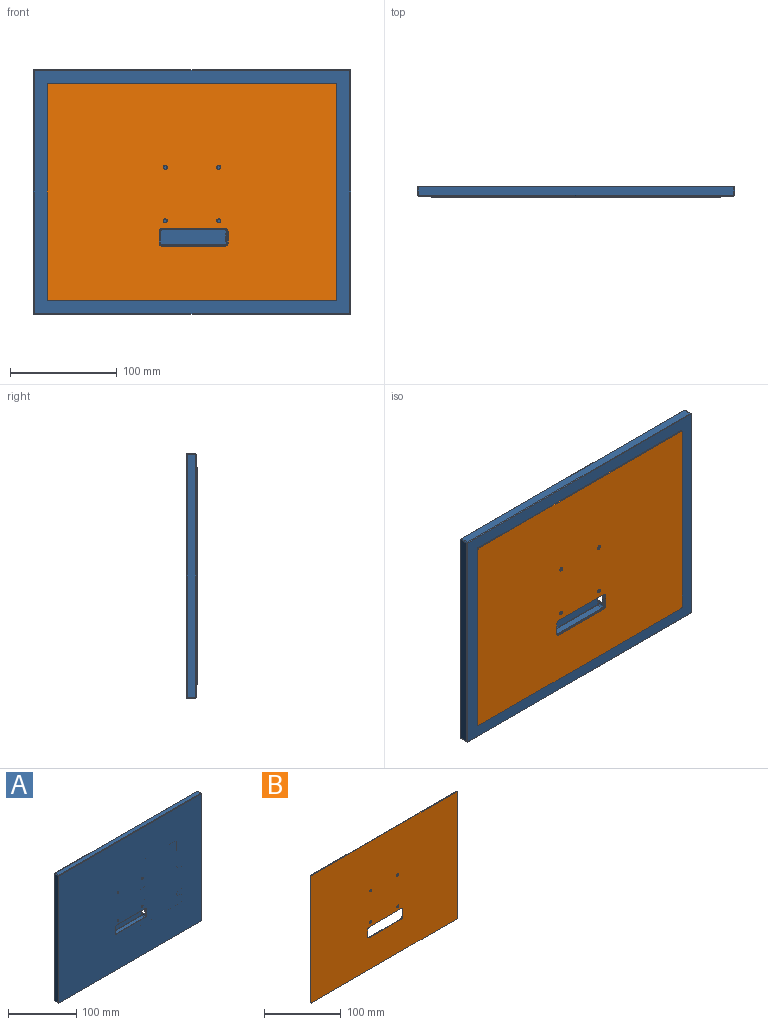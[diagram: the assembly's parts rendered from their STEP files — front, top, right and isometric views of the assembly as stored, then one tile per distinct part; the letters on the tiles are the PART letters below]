
ASSEMBLY  parts=2 mates=1
PART A: 309 faces, bbox 296.4x8.5x228.8 mm
  f0: plane 295.4x227.8mm, normal (0,-1,0), area 66249.3mm2, adj f1,f2,f3,f4,f5,f6,f7,f8
  f1: cone r=0.75mm half-angle=45deg, axis (0,1,0), area 0.8mm2, adj f0,f2,f8,f19
  f2: plane 226.8x0.5mm, normal (-0.71,-0.71,0), area 160.4mm2, adj f0,f1,f3,f20
  f3: cone r=0.75mm half-angle=45deg, axis (0,1,0), area 0.8mm2, adj f0,f2,f4,f21
  f4: plane 294.4x0.5mm, normal (0,-0.71,-0.71), area 208.2mm2, adj f0,f3,f5,f22
  f5: cone r=0.75mm half-angle=45deg, axis (0,1,0), area 0.8mm2, adj f0,f4,f6,f23
  f6: plane 226.8x0.5mm, normal (0.71,-0.71,0), area 160.4mm2, adj f0,f5,f7,f24
  f7: cone r=0.75mm half-angle=45deg, axis (0,1,0), area 0.8mm2, adj f0,f6,f8,f25
  f8: plane 294.4x0.5mm, normal (0,-0.71,0.71), area 208.2mm2, adj f0,f1,f7,f9
  f9: plane 294.4x7.9mm, normal (0,0,1), area 2325.8mm2, adj f8,f10,f19,f25
  f10: plane 294.4x0.1mm, normal (0,0.71,0.71), area 41.6mm2, adj f9,f11,f12,f18
  f11: plane 296.2x228.6mm, normal (0,1,0), area 2101.9mm2, adj f10,f12,f13,f14,f15,f16,f17,f18
  f12: cone r=0.95mm half-angle=45deg, axis (0,-1,0), area 0.2mm2, adj f10,f11,f13,f25
  f13: plane 226.8x0.1mm, normal (0.71,0.71,0), area 32.1mm2, adj f11,f12,f14,f24
  f14: cone r=0.95mm half-angle=45deg, axis (0,-1,0), area 0.2mm2, adj f11,f13,f15,f23
  f15: plane 294.4x0.1mm, normal (0,0.71,-0.71), area 41.6mm2, adj f11,f14,f16,f22
  f16: cone r=0.95mm half-angle=45deg, axis (0,-1,0), area 0.2mm2, adj f11,f15,f17,f21
  f17: plane 226.8x0.1mm, normal (-0.71,0.71,0), area 32.1mm2, adj f11,f16,f18,f20
  f18: cone r=0.95mm half-angle=45deg, axis (0,-1,0), area 0.2mm2, adj f10,f11,f17,f19
  f19: cylinder r=1mm len=7.9mm, axis (0,-1,0), area 12.4mm2, adj f1,f9,f18,f20
  f20: plane 226.8x7.9mm, normal (-1,0,0), area 1791.7mm2, adj f2,f17,f19,f21
  f21: cylinder r=1mm len=7.9mm, axis (0,-1,0), area 12.4mm2, adj f3,f16,f20,f22
  f22: plane 294.4x7.9mm, normal (0,0,-1), area 2325.8mm2, adj f4,f15,f21,f23
  f23: cylinder r=1mm len=7.9mm, axis (0,-1,0), area 12.4mm2, adj f5,f14,f22,f24
  f24: plane 226.8x7.9mm, normal (1,0,0), area 1791.7mm2, adj f6,f13,f23,f25
  f25: cylinder r=1mm len=7.9mm, axis (0,-1,0), area 12.4mm2, adj f7,f9,f12,f24
  f26: plane 34.66x6.82mm, normal (0,0,1), area 181.9mm2, adj f11,f30,f41,f150,f153,f162,f191,f196
  f27: plane 52.54x20.14mm, normal (0,1,0), area 278mm2, adj f35,f36,f38,f39,f40,f169,f187,f192
  f28: plane 41.64x20.14mm, normal (0,1,0), area 234.4mm2, adj f37,f168,f173,f174,f175,f183,f185,f186
  f29: plane 35.59x14.84mm, normal (0,1,0), area 183.9mm2, adj f50,f167,f171,f176,f177,f178,f179,f182
  f30: plane 32.68x31.26mm, normal (0,1,0), area 242.7mm2, adj f26,f150,f170,f189,f190,f191,f193,f236
  f31: plane 53.55x1.8mm, normal (0,1,0), area 92.6mm2, adj f89,f90,f92,f197
  f32: plane 29.26x2.3mm, normal (0,1,0), area 66.4mm2, adj f56,f58,f59,f60,f62,f222,f223,f224
  f33: plane 286.85x170.03mm, normal (0,1,0), area 4919.4mm2, adj f48,f51,f52,f53,f54,f55,f57,f61
  f34: plane 52.85x4.27mm, normal (0,1,0), area 217.9mm2, adj f42,f43,f44,f45,f46,f47,f49,f181
  f35: cylinder r=1mm len=5mm, axis (0,1,0), area 7.9mm2, adj f27,f36,f41,f192
  f36: plane 49.4x5mm, normal (0,0,1), area 247mm2, adj f27,f35,f38,f41
  f37: plane 38.5x5mm, normal (0,0,1), area 192.5mm2, adj f28,f41,f175,f186
  f38: cylinder r=1mm len=5mm, axis (0,-1,0), area 7.9mm2, adj f27,f36,f39,f41
  f39: plane 17.74x5mm, normal (1,0,0), area 88.7mm2, adj f27,f38,f40,f41
  f40: cylinder r=2mm len=6.72mm, axis (0,-1,0), area 18.4mm2, adj f27,f39,f41,f153,f169,f184
  f41: plane 294.43x210.78mm, normal (0,1,0), area 32643.8mm2, adj f26,f35,f36,f37,f38,f39,f40,f42
  f42: plane 5x1.37mm, normal (0,0,-1), area 6.9mm2, adj f34,f41,f43,f181
  f43: cylinder r=1mm len=5mm, axis (0,1,0), area 7.9mm2, adj f34,f41,f42,f44
  f44: plane 48.9x5mm, normal (-1,0,0), area 244.5mm2, adj f34,f41,f43,f45
  f45: cylinder r=1mm len=5mm, axis (0,-1,0), area 7.9mm2, adj f34,f41,f44,f46
  f46: plane 5x1.87mm, normal (0,0,1), area 9.4mm2, adj f34,f41,f45,f47
  f47: cylinder r=2mm len=6.82mm, axis (0,-1,0), area 18.6mm2, adj f11,f34,f41,f46,f49,f229
  f48: plane 30.66x1.82mm, normal (-1,0,0), area 55.8mm2, adj f11,f33,f51,f156
  f49: plane 52.85x1.82mm, normal (-1,0,0), area 96.2mm2, adj f11,f34,f47,f181
  f50: plane 34.09x1.82mm, normal (-1,0,0), area 62mm2, adj f11,f29,f179,f182
  f51: cylinder r=2mm len=6.82mm, axis (0,-1,0), area 18.6mm2, adj f11,f33,f41,f48,f52,f229
  f52: plane 20.87x5mm, normal (0,0,-1), area 104.4mm2, adj f33,f41,f51,f53
  f53: cylinder r=2mm len=5mm, axis (0,-1,0), area 15.7mm2, adj f33,f41,f52,f54
  f54: plane 135.45x5mm, normal (1,0,0), area 677.2mm2, adj f33,f41,f53,f55
  f55: cylinder r=1mm len=5mm, axis (0,1,0), area 7.9mm2, adj f33,f41,f54,f57
  f56: plane 27.26x5mm, normal (0,0,-1), area 136.3mm2, adj f32,f41,f58,f224
  f57: plane 46.3x5mm, normal (0,0,-1), area 231.5mm2, adj f33,f41,f55,f228
  f58: cylinder r=1mm len=5mm, axis (0,1,0), area 7.9mm2, adj f32,f41,f56,f59
  f59: plane 5x0.3mm, normal (-1,0,0), area 1.5mm2, adj f32,f41,f58,f60
  f60: cylinder r=1mm len=5mm, axis (0,-1,0), area 7.9mm2, adj f32,f41,f59,f62
  f61: plane 29.3x5.5mm, normal (0,0,1), area 161.1mm2, adj f33,f63,f65,f209
  f62: plane 34.7x5.5mm, normal (0,0,1), area 153.6mm2, adj f32,f41,f60,f65,f88,f222
  f63: cylinder r=1mm len=5.5mm, axis (0,-1,0), area 8.6mm2, adj f33,f61,f64,f65
  f64: plane 11x5.5mm, normal (-1,0,0), area 7mm2, adj f33,f41,f63,f65,f227,f228
  f65: plane 131x86mm, normal (0,1,0), area 8661.3mm2, adj f61,f62,f63,f64,f66,f67,f73,f74
  f66: cylinder r=2mm len=3mm, axis (0,1,0), area 5.6mm2, adj f65,f67,f72,f202
  f67: cylinder r=4mm len=6.5mm, axis (0,-1,0), area 31.2mm2, adj f65,f66,f68,f72,f97,f115
  f68: cylinder r=2mm len=3.5mm, axis (0,1,0), area 10mm2, adj f67,f72,f97,f113
  f69: plane 12x10.6mm, normal (0,1,0), area 72.6mm2, adj f73,f204,f205,f206,f207,f208,f210
  f70: plane 52.6x12.6mm, normal (0,1,0), area 526.7mm2, adj f73,f74,f75,f76,f77,f78,f79,f203
  f71: plane 52.6x12.4mm, normal (0,1,0), area 466.7mm2, adj f79,f80,f81,f82,f83,f84,f86,f87
  f72: plane 19.7x11.2mm, normal (0,1,0), area 96.4mm2, adj f66,f67,f68,f87,f110,f111,f112,f113
  f73: plane 112x5.5mm, normal (-1,0,0), area 428.2mm2, adj f33,f65,f69,f70,f74,f203,f204,f208
  f74: cylinder r=2mm len=3mm, axis (0,-1,0), area 9.4mm2, adj f65,f70,f73,f75
  f75: plane 4.6x3mm, normal (0,0,-1), area 13.8mm2, adj f65,f70,f74,f76
  f76: cylinder r=4mm len=4mm, axis (0,-1,0), area 18.8mm2, adj f65,f70,f75,f77
  f77: plane 44.6x3mm, normal (-1,0,0), area 133.8mm2, adj f65,f70,f76,f78
  f78: cylinder r=2mm len=3mm, axis (0,1,0), area 9.4mm2, adj f65,f70,f77,f79
  f79: plane 82x5.5mm, normal (0,0,-1), area 388mm2, adj f33,f65,f70,f71,f78,f80,f198,f203
  f80: cylinder r=2mm len=3mm, axis (0,-1,0), area 9.4mm2, adj f65,f71,f79,f81
  f81: plane 44.6x3mm, normal (1,0,0), area 133.8mm2, adj f65,f71,f80,f82
  f82: cylinder r=4mm len=4mm, axis (0,-1,0), area 18.8mm2, adj f65,f71,f81,f83
  f83: plane 4.4x3mm, normal (0,0,-1), area 13.2mm2, adj f65,f71,f82,f84
  f84: cylinder r=2mm len=3mm, axis (0,1,0), area 9.4mm2, adj f65,f71,f83,f87
  f85: plane 4.5x0.5mm, normal (1,0,0), area 2.3mm2, adj f41,f65,f88,f89
  f86: plane 25.2x2.5mm, normal (1,0,0), area 63mm2, adj f33,f71,f105,f198
  f87: plane 39x5.5mm, normal (1,0,0), area 148.5mm2, adj f33,f65,f71,f72,f84,f102,f111,f199
  f88: cylinder r=2mm len=2mm, axis (0,-1,0), area 1.6mm2, adj f41,f62,f65,f85
  f89: cylinder r=2mm len=5.5mm, axis (0,1,0), area 16.3mm2, adj f31,f41,f65,f85,f90,f197
  f90: plane 60.36x6.5mm, normal (0,0,-1), area 97.8mm2, adj f31,f65,f89,f91,f93,f97,f114
  f91: plane 0.21x0.01mm, normal (0,-1,0), area 0mm2, adj f90,f92,f93
  f92: cylinder r=2mm len=5mm, axis (0,-1,0), area 15.7mm2, adj f31,f41,f91,f93,f197
  f93: plane 151.21x6mm, normal (-1,0,0), area 774mm2, adj f33,f41,f90,f91,f92,f97,f108,f148
  f94: plane 7x7mm, normal (0,1,0), area 38.5mm2, adj f98
  f95: plane 7x7mm, normal (0,1,0), area 38.5mm2, adj f99
  f96: plane 7.64x7mm, normal (0,1,0), area 43mm2, adj f100,f101,f103,f104
  f97: plane 64.36x28.31mm, normal (0,1,0), area 1266.9mm2, adj f67,f68,f90,f93,f106,f107,f108,f109
  f98: cylinder r=3.5mm len=7mm, axis (0,1,0), area 22mm2, adj f33,f94
  f99: cylinder r=3.5mm len=7mm, axis (0,1,0), area 22mm2, adj f33,f95
  f100: cylinder r=3.5mm len=7mm, axis (0,-1,0), area 11mm2, adj f33,f96,f101,f104
  f101: plane 3.5x2.14mm, normal (0,0,-1), area 6mm2, adj f33,f71,f96,f100,f102,f103
  f102: cylinder r=2mm len=2.5mm, axis (0,1,0), area 7.9mm2, adj f33,f71,f87,f101
  f103: cylinder r=3.5mm len=7mm, axis (0,1,0), area 38.5mm2, adj f71,f96,f101,f104
  f104: plane 3.5x2.14mm, normal (0,0,1), area 6mm2, adj f33,f71,f96,f100,f103,f105
  f105: cylinder r=2mm len=2.5mm, axis (0,-1,0), area 7.9mm2, adj f33,f71,f86,f104
  f106: plane 3.81x1mm, normal (-1,0,0), area 3.8mm2, adj f33,f97,f107,f109
  f107: cylinder r=2mm len=2mm, axis (0,-1,0), area 3.1mm2, adj f33,f97,f106,f108
  f108: plane 49.56x1mm, normal (0,0,1), area 49.6mm2, adj f33,f93,f97,f107
  f109: cylinder r=3.5mm len=3.5mm, axis (0,-1,0), area 5.5mm2, adj f33,f97,f106,f110
  f110: plane 3.5x2.14mm, normal (0,0,1), area 6mm2, adj f33,f72,f97,f109,f111,f112
  f111: cylinder r=2mm len=2.5mm, axis (0,-1,0), area 7.9mm2, adj f33,f72,f87,f110
  f112: cylinder r=3.5mm len=3.5mm, axis (0,1,0), area 19.2mm2, adj f72,f97,f110,f113
  f113: plane 3.86x3.5mm, normal (1,0,0), area 13.5mm2, adj f68,f72,f97,f112
  f114: cylinder r=4mm len=6.5mm, axis (0,-1,0), area 40.8mm2, adj f65,f90,f97,f115
  f115: plane 11x6.5mm, normal (1,0,0), area 28.6mm2, adj f65,f67,f97,f114,f116,f133,f147
  f116: plane 8.5x1mm, normal (0,1,0), area 8.5mm2, adj f115,f117,f133,f147
  f117: plane 11x6.18mm, normal (-1,0,0), area 33.6mm2, adj f116,f118,f126,f128,f131,f133,f136,f147
  f118: plane 11x0.5mm, normal (-0.71,-0.71,0), area 7.8mm2, adj f0,f117,f119,f125
  f119: cone r=2.25mm half-angle=45deg, axis (0,-1,0), area 2.5mm2, adj f0,f118,f120,f136
  f120: plane 58.36x0.5mm, normal (0,-0.71,0.71), area 41.3mm2, adj f0,f119,f121,f137
  f121: cone r=2.25mm half-angle=45deg, axis (0,-1,0), area 2.5mm2, adj f0,f120,f122,f138
  f122: plane 11x0.5mm, normal (0.71,-0.71,0), area 7.8mm2, adj f0,f121,f123,f139
  f123: cone r=2.25mm half-angle=45deg, axis (0,-1,0), area 2.5mm2, adj f0,f122,f124,f140
  f124: plane 58.36x0.5mm, normal (0,-0.71,-0.71), area 41.3mm2, adj f0,f123,f125,f141
  f125: cone r=2.25mm half-angle=45deg, axis (0,-1,0), area 2.5mm2, adj f0,f118,f124,f126
  f126: cylinder r=2mm len=6.18mm, axis (0,1,0), area 19.4mm2, adj f117,f125,f127,f141
  f127: torus R=1.5mm, axis (0,1,0), area 2.2mm2, adj f126,f128,f130,f142
  f128: cylinder r=0.5mm len=1.38mm, axis (0,0,1), area 1mm2, adj f117,f127,f129,f130
  f129: cylinder r=1mm len=1mm, axis (0,-1,0), area 0.8mm2, adj f97,f128,f130,f134,f147
  f130: plane 61.36x14mm, normal (0,-1,0), area 853.2mm2, adj f127,f128,f129,f131,f132,f134,f135,f142
  f131: cylinder r=0.5mm len=1.38mm, axis (0,0,1), area 1mm2, adj f117,f130,f132,f135
  f132: cylinder r=1mm len=1mm, axis (0,-1,0), area 0.8mm2, adj f97,f130,f131,f133,f134
  f133: plane 5.05x1mm, normal (0,0,1), area 5.1mm2, adj f97,f115,f116,f117,f132
  f134: plane 6.5x0.5mm, normal (1,0,0), area 3.3mm2, adj f97,f129,f130,f132
  f135: torus R=1.5mm, axis (0,1,0), area 2.2mm2, adj f130,f131,f136,f146
  f136: cylinder r=2mm len=6.18mm, axis (0,1,0), area 19.4mm2, adj f117,f119,f135,f137
  f137: plane 58.36x6.18mm, normal (0,0,1), area 360.7mm2, adj f120,f136,f138,f146
  f138: cylinder r=2mm len=6.18mm, axis (0,-1,0), area 19.4mm2, adj f121,f137,f139,f145
  f139: plane 11x6.18mm, normal (1,0,0), area 68mm2, adj f122,f138,f140,f144
  f140: cylinder r=2mm len=6.18mm, axis (0,-1,0), area 19.4mm2, adj f123,f139,f141,f143
  f141: plane 58.36x6.18mm, normal (0,0,-1), area 360.7mm2, adj f124,f126,f140,f142
  f142: cylinder r=0.5mm len=58.36mm, axis (-1,0,0), area 45.8mm2, adj f127,f130,f141,f143
  f143: torus R=1.5mm, axis (0,-1,0), area 2.2mm2, adj f130,f140,f142,f144
  f144: cylinder r=0.5mm len=11mm, axis (0,0,-1), area 8.6mm2, adj f130,f139,f143,f145
  f145: torus R=1.5mm, axis (0,-1,0), area 2.2mm2, adj f130,f138,f144,f146
  f146: cylinder r=0.5mm len=58.36mm, axis (1,0,0), area 45.8mm2, adj f130,f135,f137,f145
  f147: plane 5.05x1mm, normal (0,0,-1), area 5.1mm2, adj f97,f115,f116,f117,f129
  f148: cylinder r=2mm len=5mm, axis (0,-1,0), area 15.7mm2, adj f33,f41,f93,f149
  f149: plane 112x6.82mm, normal (0,0,-1), area 568.6mm2, adj f11,f33,f41,f148,f151,f152,f161,f194
  f150: plane 31.18x1.72mm, normal (1,0,0), area 53.6mm2, adj f26,f30,f153,f193
  f151: plane 4.53x1.72mm, normal (1,0,0), area 7.8mm2, adj f33,f149,f152,f154
  f152: plane 286.35x9.03mm, normal (0,1,0), area 1303.7mm2, adj f149,f151,f154,f155,f157,f158,f159,f160
  f153: plane 286.35x35.68mm, normal (0,1,0), area 1337.3mm2, adj f26,f40,f150,f162,f163,f164,f165,f166
  f154: cylinder r=1.5mm len=3mm, axis (0,1,0), area 8.1mm2, adj f33,f151,f152,f155
  f155: plane 280.85x1.82mm, normal (0,0,-1), area 483.3mm2, adj f11,f33,f152,f154,f156,f157
  f156: cylinder r=1.5mm len=3mm, axis (0,1,0), area 8.6mm2, adj f11,f33,f48,f155
  f157: plane 2.5x0.1mm, normal (-1,0,0), area 0.3mm2, adj f11,f152,f155,f158
  f158: cylinder r=2mm len=2mm, axis (0,-1,0), area 0.3mm2, adj f11,f152,f157,f159
  f159: plane 282.35x0.1mm, normal (0,0,-1), area 28.2mm2, adj f11,f152,f158,f160
  f160: cylinder r=2mm len=2mm, axis (0,-1,0), area 0.3mm2, adj f11,f152,f159,f161
  f161: plane 7.03x0.1mm, normal (1,0,0), area 0.7mm2, adj f11,f149,f152,f160
  f162: plane 33.68x0.1mm, normal (1,0,0), area 3.4mm2, adj f11,f26,f153,f163
  f163: cylinder r=2mm len=2mm, axis (0,-1,0), area 0.3mm2, adj f11,f153,f162,f164
  f164: plane 282.35x0.1mm, normal (0,0,1), area 28.2mm2, adj f11,f153,f163,f165
  f165: cylinder r=2mm len=2mm, axis (0,-1,0), area 0.3mm2, adj f11,f153,f164,f166
  f166: plane 2.5x0.1mm, normal (-1,0,0), area 0.3mm2, adj f11,f153,f165,f167
  f167: plane 11.84x1.82mm, normal (0,0,1), area 20.6mm2, adj f11,f29,f153,f166,f171,f182
  f168: plane 41.64x1.72mm, normal (0,0,1), area 71.6mm2, adj f28,f153,f173,f183
  f169: plane 52.54x1.72mm, normal (0,0,1), area 90.4mm2, adj f27,f40,f153,f187
  f170: plane 28.26x1.72mm, normal (0,0,1), area 48.6mm2, adj f30,f153,f189,f193
  f171: cylinder r=2mm len=6.72mm, axis (0,-1,0), area 18.4mm2, adj f29,f41,f153,f167,f172,f176
  f172: plane 46x6.72mm, normal (0,0,1), area 309.1mm2, adj f41,f153,f171,f173
  f173: cylinder r=2mm len=6.72mm, axis (0,-1,0), area 18.4mm2, adj f28,f41,f153,f168,f172,f174
  f174: plane 17.74x5mm, normal (1,0,0), area 88.7mm2, adj f28,f41,f173,f175
  f175: cylinder r=1mm len=5mm, axis (0,-1,0), area 7.9mm2, adj f28,f37,f41,f174
  f176: plane 30.32x5mm, normal (-1,0,0), area 151.6mm2, adj f29,f41,f171,f177
  f177: cylinder r=1mm len=5mm, axis (0,-1,0), area 7.9mm2, adj f29,f41,f176,f178
  f178: plane 11.37x5mm, normal (0,0,1), area 56.8mm2, adj f29,f41,f177,f179
  f179: cylinder r=2mm len=6.82mm, axis (0,-1,0), area 16.9mm2, adj f11,f29,f41,f50,f178,f180
  f180: plane 46.5x6.82mm, normal (-1,0,0), area 317.1mm2, adj f11,f41,f179,f181
  f181: cylinder r=2mm len=6.82mm, axis (0,-1,0), area 16.9mm2, adj f11,f34,f41,f42,f49,f180
  f182: cylinder r=1.5mm len=3mm, axis (0,1,0), area 8.6mm2, adj f11,f29,f50,f167
  f183: cylinder r=2mm len=6.72mm, axis (0,-1,0), area 18.4mm2, adj f28,f41,f153,f168,f184,f185
  f184: plane 46x6.72mm, normal (0,0,1), area 309.1mm2, adj f40,f41,f153,f183
  f185: plane 17.74x5mm, normal (-1,0,0), area 88.7mm2, adj f28,f41,f183,f186
  f186: cylinder r=1mm len=5mm, axis (0,1,0), area 7.9mm2, adj f28,f37,f41,f185
  f187: cylinder r=2mm len=6.72mm, axis (0,-1,0), area 18.4mm2, adj f27,f41,f153,f169,f188,f192
  f188: plane 46x6.72mm, normal (0,0,1), area 309.1mm2, adj f41,f153,f187,f189
  f189: cylinder r=2mm len=6.72mm, axis (0,-1,0), area 18.4mm2, adj f30,f41,f153,f170,f188,f190
  f190: plane 28.78x5mm, normal (1,0,0), area 143.9mm2, adj f30,f41,f189,f191
  f191: cylinder r=1mm len=5mm, axis (0,1,0), area 7.9mm2, adj f26,f30,f41,f190
  f192: plane 17.74x5mm, normal (-1,0,0), area 88.7mm2, adj f27,f35,f41,f187
  f193: cylinder r=1.5mm len=3mm, axis (0,1,0), area 8.1mm2, adj f30,f150,f153,f170
  f194: cylinder r=2mm len=6.82mm, axis (0,-1,0), area 21.4mm2, adj f11,f41,f149,f195
  f195: plane 175x6.82mm, normal (1,0,0), area 1193.5mm2, adj f11,f41,f194,f196
  f196: cylinder r=2mm len=6.82mm, axis (0,-1,0), area 21.4mm2, adj f11,f26,f41,f195
  f197: plane 49.57x5mm, normal (0,0,-1), area 247.9mm2, adj f31,f41,f89,f92
  f198: cylinder r=2mm len=2.5mm, axis (0,-1,0), area 7.9mm2, adj f33,f71,f79,f86
  f199: cylinder r=2mm len=3mm, axis (0,-1,0), area 9.4mm2, adj f65,f72,f87,f200
  f200: plane 4.4x3mm, normal (0,0,1), area 13.2mm2, adj f65,f72,f199,f201
  f201: cylinder r=4mm len=4mm, axis (0,-1,0), area 18.8mm2, adj f65,f72,f200,f202
  f202: plane 12.1x3mm, normal (1,0,0), area 36.3mm2, adj f65,f66,f72,f201
  f203: cylinder r=2mm len=2.5mm, axis (0,-1,0), area 7.9mm2, adj f33,f70,f73,f79
  f204: cylinder r=2mm len=3mm, axis (0,1,0), area 9.4mm2, adj f65,f69,f73,f205
  f205: plane 4.6x3mm, normal (0,0,1), area 13.8mm2, adj f65,f69,f204,f206
  f206: cylinder r=4mm len=8mm, axis (0,-1,0), area 37.7mm2, adj f65,f69,f205,f207
  f207: plane 4.6x3mm, normal (0,0,-1), area 13.8mm2, adj f65,f69,f206,f208
  f208: cylinder r=2mm len=3mm, axis (0,-1,0), area 9.4mm2, adj f65,f69,f73,f207
  f209: cylinder r=2mm len=5.5mm, axis (0,-1,0), area 17.3mm2, adj f33,f61,f65,f73
  f210: cylinder r=1.5mm len=3mm, axis (0,1,0), area 18.8mm2, adj f69,f211
  f211: cone r=1.25mm half-angle=45deg, axis (0,-1,0), area 5.6mm2, adj f210,f215
  f212: plane 2x2mm, normal (0,1,0), area 3.1mm2, adj f216
  f213: plane 2x2mm, normal (0,1,0), area 3.1mm2, adj f218
  f214: plane 2x2mm, normal (0,1,0), area 3.1mm2, adj f220
  f215: plane 2x2mm, normal (0,1,0), area 3.1mm2, adj f211
  f216: cone r=1.25mm half-angle=45deg, axis (0,-1,0), area 5.6mm2, adj f212,f217
  f217: cylinder r=1.5mm len=3mm, axis (0,1,0), area 18.8mm2, adj f71,f216
  f218: cone r=1.25mm half-angle=45deg, axis (0,-1,0), area 5.6mm2, adj f213,f219
  f219: cylinder r=1.5mm len=3mm, axis (0,1,0), area 18.8mm2, adj f72,f218
  f220: cone r=1.25mm half-angle=45deg, axis (0,-1,0), area 5.6mm2, adj f214,f221
  f221: cylinder r=1.5mm len=3mm, axis (0,1,0), area 18.8mm2, adj f70,f220
  f222: cylinder r=1mm len=5.5mm, axis (0,1,0), area 8.6mm2, adj f32,f62,f65,f223
  f223: plane 11x5.5mm, normal (1,0,0), area 7mm2, adj f32,f41,f65,f222,f224,f225
  f224: cylinder r=1mm len=5mm, axis (0,-1,0), area 7.9mm2, adj f32,f41,f56,f223
  f225: cylinder r=3mm len=3mm, axis (0,-1,0), area 2.4mm2, adj f41,f65,f223,f226
  f226: plane 10x0.5mm, normal (0,0,1), area 5mm2, adj f41,f65,f225,f227
  f227: cylinder r=3mm len=3mm, axis (0,-1,0), area 2.4mm2, adj f41,f64,f65,f226
  f228: cylinder r=1mm len=5mm, axis (0,1,0), area 7.9mm2, adj f33,f41,f57,f64
  f229: plane 46.5x6.82mm, normal (-1,0,0), area 317.1mm2, adj f11,f41,f47,f51
  f230: plane 41.4x5mm, normal (0,0,1), area 207mm2, adj f27,f231,f233,f244
  f231: cylinder r=3mm len=5mm, axis (0,-1,0), area 23.6mm2, adj f27,f230,f233,f249
  f232: plane 27.18x26.69mm, normal (0,1,0), area 717.4mm2, adj f236,f237,f238,f239,f240,f241,f242,f243
  f233: plane 47.4x16.14mm, normal (0,1,0), area 757.3mm2, adj f230,f231,f244,f245,f246,f247,f248,f249
  f234: plane 36.5x16.14mm, normal (0,1,0), area 581.4mm2, adj f250,f251,f252,f253,f254,f255,f256,f257
  f235: plane 28.72x10.27mm, normal (0,1,0), area 287mm2, adj f258,f259,f260,f261,f262,f263,f264,f265
  f236: cylinder r=3mm len=5mm, axis (0,-1,0), area 23.6mm2, adj f30,f232,f237,f243
  f237: plane 20.69x5mm, normal (0,0,-1), area 103.4mm2, adj f30,f232,f236,f238
  f238: cylinder r=3mm len=5mm, axis (0,-1,0), area 23.6mm2, adj f30,f232,f237,f239
  f239: plane 21.18x5mm, normal (-1,0,0), area 105.9mm2, adj f30,f232,f238,f240
  f240: cylinder r=3mm len=5mm, axis (0,-1,0), area 23.6mm2, adj f30,f232,f239,f241
  f241: plane 20.69x5mm, normal (0,0,1), area 103.4mm2, adj f30,f232,f240,f242
  f242: cylinder r=3mm len=5mm, axis (0,-1,0), area 23.6mm2, adj f30,f232,f241,f243
  f243: plane 21.18x5mm, normal (1,0,0), area 105.9mm2, adj f30,f232,f236,f242
  f244: cylinder r=3mm len=5mm, axis (0,-1,0), area 23.6mm2, adj f27,f230,f233,f245
  f245: plane 10.14x5mm, normal (-1,0,0), area 50.7mm2, adj f27,f233,f244,f246
  f246: cylinder r=3mm len=5mm, axis (0,-1,0), area 23.6mm2, adj f27,f233,f245,f247
  f247: plane 41.4x5mm, normal (0,0,-1), area 207mm2, adj f27,f233,f246,f248
  f248: cylinder r=3mm len=5mm, axis (0,-1,0), area 23.6mm2, adj f27,f233,f247,f249
  f249: plane 10.14x5mm, normal (1,0,0), area 50.7mm2, adj f27,f231,f233,f248
  f250: cylinder r=3mm len=5mm, axis (0,-1,0), area 23.6mm2, adj f28,f234,f251,f257
  f251: plane 10.14x5mm, normal (1,0,0), area 50.7mm2, adj f28,f234,f250,f252
  f252: cylinder r=3mm len=5mm, axis (0,-1,0), area 23.6mm2, adj f28,f234,f251,f253
  f253: plane 30.5x5mm, normal (0,0,-1), area 152.5mm2, adj f28,f234,f252,f254
  f254: cylinder r=3mm len=5mm, axis (0,-1,0), area 23.6mm2, adj f28,f234,f253,f255
  f255: plane 10.14x5mm, normal (-1,0,0), area 50.7mm2, adj f28,f234,f254,f256
  f256: cylinder r=3mm len=5mm, axis (0,-1,0), area 23.6mm2, adj f28,f234,f255,f257
  f257: plane 30.5x5mm, normal (0,0,1), area 152.5mm2, adj f28,f234,f250,f256
  f258: cylinder r=3mm len=5mm, axis (0,-1,0), area 23.6mm2, adj f29,f235,f259,f265
  f259: plane 5x4.27mm, normal (0,0,1), area 21.3mm2, adj f29,f235,f258,f260
  f260: cylinder r=3mm len=5mm, axis (0,-1,0), area 23.6mm2, adj f29,f235,f259,f261
  f261: plane 22.72x5mm, normal (1,0,0), area 113.6mm2, adj f29,f235,f260,f262
  f262: cylinder r=3mm len=5mm, axis (0,-1,0), area 23.6mm2, adj f29,f235,f261,f263
  f263: plane 5x4.27mm, normal (0,0,-1), area 21.3mm2, adj f29,f235,f262,f264
  f264: cylinder r=3mm len=5mm, axis (0,-1,0), area 23.6mm2, adj f29,f235,f263,f265
  f265: plane 22.72x5mm, normal (-1,0,0), area 113.6mm2, adj f29,f235,f258,f264
  f266: plane 28.2x5mm, normal (-1,0,0), area 141mm2, adj f33,f268,f269,f284
  f267: plane 41.31x5mm, normal (-1,0,0), area 206.5mm2, adj f33,f270,f287,f290
  f268: cylinder r=3mm len=5mm, axis (0,1,0), area 23.6mm2, adj f33,f266,f269,f291
  f269: plane 162.83x74.9mm, normal (0,1,0), area 7381.3mm2, adj f266,f268,f271,f272,f274,f275,f276,f277
  f270: plane 47.31x36.56mm, normal (0,1,0), area 1721.7mm2, adj f267,f273,f285,f286,f287,f288,f289,f290
  f271: cylinder r=3mm len=5mm, axis (0,-1,0), area 23.6mm2, adj f33,f269,f272,f291
  f272: plane 68.9x5mm, normal (1,0,0), area 344.5mm2, adj f33,f269,f271,f274
  f273: plane 41.31x5mm, normal (1,0,0), area 206.5mm2, adj f33,f270,f285,f288
  f274: cylinder r=3mm len=5mm, axis (0,-1,0), area 23.6mm2, adj f33,f269,f272,f275
  f275: plane 156.83x5mm, normal (0,0,-1), area 784.1mm2, adj f33,f269,f274,f276
  f276: cylinder r=3mm len=5mm, axis (0,-1,0), area 23.6mm2, adj f33,f269,f275,f277
  f277: plane 14.56x5mm, normal (-1,0,0), area 72.8mm2, adj f33,f269,f276,f278
  f278: cylinder r=3mm len=5mm, axis (0,-1,0), area 23.6mm2, adj f33,f269,f277,f279
  f279: plane 18.27x5mm, normal (0,0,1), area 91.4mm2, adj f33,f269,f278,f280
  f280: cylinder r=3mm len=5mm, axis (0,1,0), area 23.6mm2, adj f33,f269,f279,f281
  f281: plane 14.15x5mm, normal (-1,0,0), area 70.7mm2, adj f33,f269,f280,f282
  f282: cylinder r=3mm len=5mm, axis (0,-1,0), area 23.6mm2, adj f33,f269,f281,f283
  f283: plane 96x5mm, normal (0,0,1), area 480mm2, adj f33,f269,f282,f284
  f284: cylinder r=3mm len=5mm, axis (0,1,0), area 23.6mm2, adj f33,f266,f269,f283
  f285: cylinder r=3mm len=5mm, axis (0,1,0), area 23.6mm2, adj f33,f270,f273,f286
  f286: plane 30.56x5mm, normal (0,0,-1), area 152.8mm2, adj f33,f270,f285,f287
  f287: cylinder r=3mm len=5mm, axis (0,-1,0), area 23.6mm2, adj f33,f267,f270,f286
  f288: cylinder r=3mm len=5mm, axis (0,-1,0), area 23.6mm2, adj f33,f270,f273,f289
  f289: plane 30.56x5mm, normal (0,0,1), area 152.8mm2, adj f33,f270,f288,f290
  f290: cylinder r=3mm len=5mm, axis (0,-1,0), area 23.6mm2, adj f33,f267,f270,f289
  f291: plane 30.56x5mm, normal (0,0,1), area 152.8mm2, adj f33,f268,f269,f271
  f292: plane 6x5mm, normal (0,0,-1), area 30mm2, adj f33,f293,f294,f300
  f293: cylinder r=3mm len=5mm, axis (0,-1,0), area 23.6mm2, adj f33,f292,f294,f295
  f294: plane 116.3x12mm, normal (0,1,0), area 1387.3mm2, adj f292,f293,f295,f296,f297,f298,f299,f300
  f295: plane 110.3x5mm, normal (1,0,0), area 551.5mm2, adj f33,f293,f294,f296
  f296: cylinder r=3mm len=5mm, axis (0,-1,0), area 23.6mm2, adj f33,f294,f295,f297
  f297: plane 6x5mm, normal (0,0,1), area 30mm2, adj f33,f294,f296,f298
  f298: cylinder r=3mm len=5mm, axis (0,-1,0), area 23.6mm2, adj f33,f294,f297,f299
  f299: plane 110.3x5mm, normal (-1,0,0), area 551.5mm2, adj f33,f294,f298,f300
  f300: cylinder r=3mm len=5mm, axis (0,-1,0), area 23.6mm2, adj f33,f292,f294,f299
  f301: cylinder r=1.65mm len=7mm, axis (0,-1,0), area 72.6mm2, adj f0,f302
  f302: plane 3.3x3.3mm, normal (0,-1,0), area 8.6mm2, adj f301
  f303: cylinder r=1.65mm len=7mm, axis (0,-1,0), area 72.6mm2, adj f0,f304
  f304: plane 3.3x3.3mm, normal (0,-1,0), area 8.6mm2, adj f303
  f305: cylinder r=1.65mm len=7mm, axis (0,-1,0), area 72.6mm2, adj f0,f306
  f306: plane 3.3x3.3mm, normal (0,-1,0), area 8.6mm2, adj f305
  f307: cylinder r=1.65mm len=7mm, axis (0,-1,0), area 72.6mm2, adj f0,f308
  f308: plane 3.3x3.3mm, normal (0,-1,0), area 8.6mm2, adj f307
PART B: 22 faces, bbox 270.4x1x202.8 mm
  f0: plane 270.4x202.8mm, normal (0,-1,0), area 53704.5mm2, adj f1,f2,f3,f4,f6,f7,f8,f9
  f1: plane 268.4x1mm, normal (0,0,-1), area 268.4mm2, adj f0,f5,f6,f9
  f2: plane 200.8x1mm, normal (1,0,0), area 200.8mm2, adj f0,f5,f6,f7
  f3: plane 268.4x1mm, normal (0,0,1), area 268.4mm2, adj f0,f5,f7,f8
  f4: plane 200.8x1mm, normal (-1,0,0), area 200.8mm2, adj f0,f5,f8,f9
  f5: plane 270.4x202.8mm, normal (0,1,0), area 53704.5mm2, adj f1,f2,f3,f4,f6,f7,f8,f9
  f6: cylinder r=1mm len=1mm, axis (0,1,0), area 1.6mm2, adj f0,f1,f2,f5
  f7: cylinder r=1mm len=1mm, axis (0,-1,0), area 1.6mm2, adj f0,f2,f3,f5
  f8: cylinder r=1mm len=1mm, axis (0,1,0), area 1.6mm2, adj f0,f3,f4,f5
  f9: cylinder r=1mm len=1mm, axis (0,-1,0), area 1.6mm2, adj f0,f1,f4,f5
  f10: cylinder r=1.9mm len=3.8mm, axis (0,-1,0), area 11.9mm2, adj f0,f5
  f11: cylinder r=3mm len=3mm, axis (0,-1,0), area 4.7mm2, adj f0,f5,f12,f18
  f12: plane 58.36x1mm, normal (0,0,1), area 58.4mm2, adj f0,f5,f11,f13
  f13: cylinder r=3mm len=3mm, axis (0,-1,0), area 4.7mm2, adj f0,f5,f12,f14
  f14: plane 11x1mm, normal (-1,0,0), area 11mm2, adj f0,f5,f13,f15
  f15: cylinder r=3mm len=3mm, axis (0,-1,0), area 4.7mm2, adj f0,f5,f14,f16
  f16: plane 58.36x1mm, normal (0,0,-1), area 58.4mm2, adj f0,f5,f15,f17
  f17: cylinder r=3mm len=3mm, axis (0,-1,0), area 4.7mm2, adj f0,f5,f16,f18
  f18: plane 11x1mm, normal (1,0,0), area 11mm2, adj f0,f5,f11,f17
  f19: cylinder r=1.9mm len=3.8mm, axis (0,-1,0), area 11.9mm2, adj f0,f5
  f20: cylinder r=1.9mm len=3.8mm, axis (0,-1,0), area 11.9mm2, adj f0,f5
  f21: cylinder r=1.9mm len=3.8mm, axis (0,-1,0), area 11.9mm2, adj f0,f5
PLACE A t=(0.02,0,-0.64)mm
PLACE B t=(0.02,0,-0.64)mm
MATE fastened A.f0 <-> B.f5  axis (0,-1,0) through (-147.68,0,-0.64)mm
